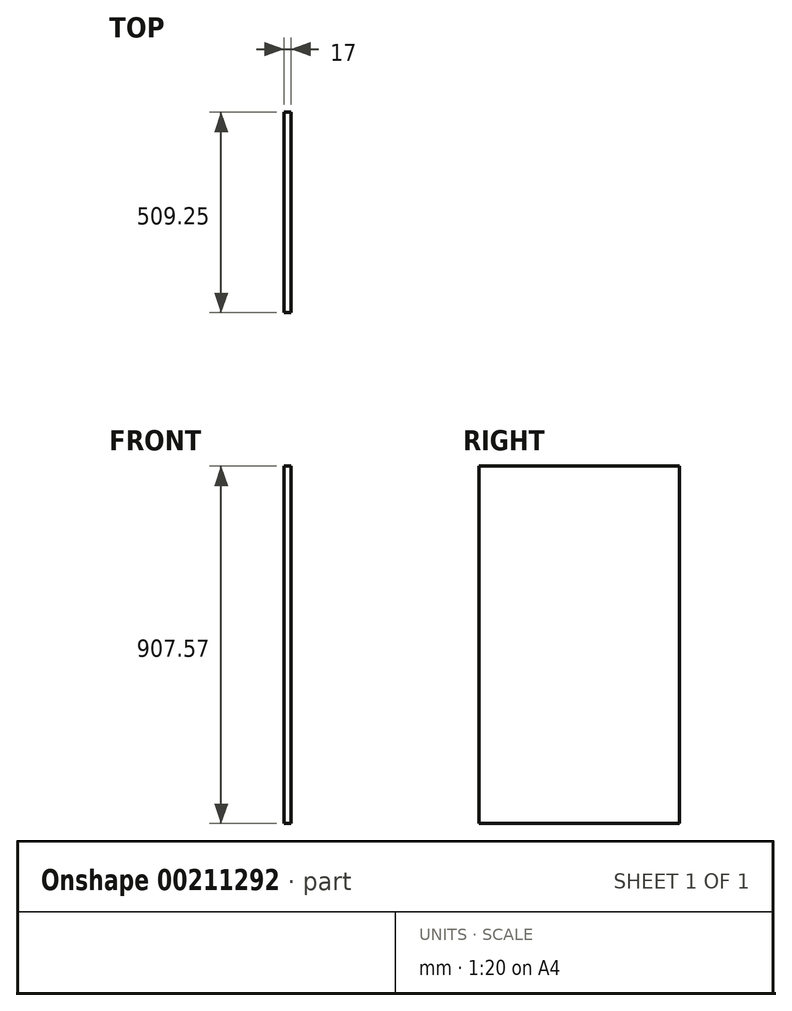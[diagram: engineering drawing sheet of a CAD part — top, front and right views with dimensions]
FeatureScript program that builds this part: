
annotation { "Feature Type Name" : "Feature", "Feature Type Description" : "" }
export const myFeature = defineFeature(function(context is Context, id is Id, definition is map)
    precondition{}
    {
        {
            var Q0;
            Q0=qCreatedBy(makeId("Right.planeOp"),FACE);
            var sketch = newSketch(context, id + "F0", { "sketchPlane" : qUnion([Q0])});
            skLineSegment(sketch, "E0.bottom", {"start": v(1067.35, 760.38) * mm, "end": v(558.1, 760.38) * mm});
            skLineSegment(sketch, "E0.top", {"start": v(1067.35, -147.2) * mm, "end": v(558.1, -147.2) * mm});
            skLineSegment(sketch, "E0.left", {"start": v(1067.35, 760.38) * mm, "end": v(1067.35, -147.2) * mm});
            skLineSegment(sketch, "E0.right", {"start": v(558.1, 760.38) * mm, "end": v(558.1, -147.2) * mm});
            skSolve(sketch);
        }
        {
            var Q0;
            Q0=makeQuery(id+"F0.imprint","IMPRINT",FACE,{"disambiguationData":[TD([[makeQuery(id+"F0.imprint","IMPRINT",EDGE,{"derivedFrom":sQuery(id+"F0.wireOp",EDGE,"E0.bottom")}),1.0]])]});
            extrude(context, id + "F1", {"entities" : qUnion([Q0]), "depth" : 17 * mm});
        }
    });
